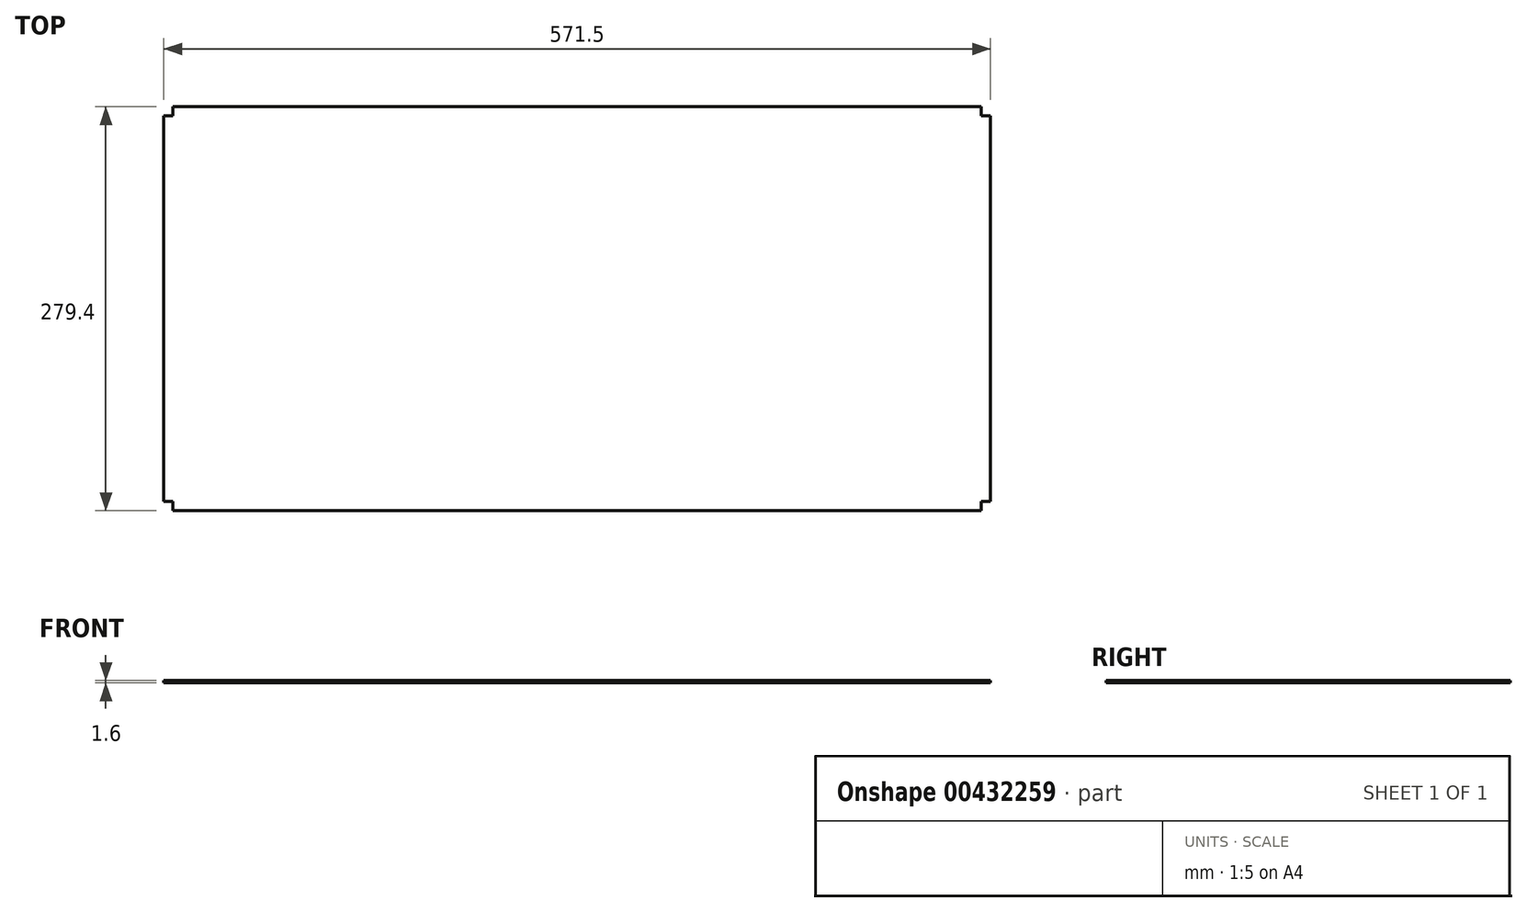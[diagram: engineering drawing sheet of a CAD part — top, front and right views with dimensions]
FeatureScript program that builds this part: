
annotation { "Feature Type Name" : "Feature", "Feature Type Description" : "" }
export const myFeature = defineFeature(function(context is Context, id is Id, definition is map)
    precondition{}
    {
        {
            var Q0;
            Q0=qCreatedBy(makeId("Top.planeOp"),FACE);
            var sketch = newSketch(context, id + "F0", { "sketchPlane" : qUnion([Q0])});
            skLineSegment(sketch, "E0.bottom", {"start": v(279.4, 139.7) * mm, "end": v(-279.4, 139.7) * mm});
            skLineSegment(sketch, "E0.top", {"start": v(279.4, -139.7) * mm, "end": v(-279.4, -139.7) * mm});
            skLineSegment(sketch, "E0.left", {"start": v(285.75, 133.35) * mm, "end": v(285.75, -133.35) * mm});
            skLineSegment(sketch, "E0.right", {"start": v(-285.75, 127) * mm, "end": v(-285.75, -133.35) * mm});
            skPoint(sketch, "E0.middle", {"position": v(0, 0) * mm});
            skPoint(sketch, "E1.orphan", {"position": v(285.75, 139.7) * mm});
            skPoint(sketch, "E2.orphan", {"position": v(-285.75, 139.7) * mm});
            skLineSegment(sketch, "E3.top", {"start": v(-285.75, -133.35) * mm, "end": v(-279.4, -133.35) * mm});
            skLineSegment(sketch, "E3.right", {"start": v(-279.4, -139.7) * mm, "end": v(-279.4, -133.35) * mm});
            skLineSegment(sketch, "E4.top", {"start": v(285.75, -133.35) * mm, "end": v(279.4, -133.35) * mm});
            skLineSegment(sketch, "E4.right", {"start": v(279.4, -139.7) * mm, "end": v(279.4, -133.35) * mm});
            skPoint(sketch, "E4.left.start.orphan", {"position": v(285.75, -139.7) * mm});
            skPoint(sketch, "E5.orphan", {"position": v(-285.75, -139.7) * mm});
            skLineSegment(sketch, "E6.top", {"start": v(-285.75, 133.35) * mm, "end": v(-279.4, 133.35) * mm});
            skLineSegment(sketch, "E6.right", {"start": v(-279.4, 139.7) * mm, "end": v(-279.4, 133.35) * mm});
            skPoint(sketch, "E7.oppositeSnap0", {"position": v(-282.57, 133.35) * mm});
            skLineSegment(sketch, "E7.top", {"start": v(285.75, 133.35) * mm, "end": v(279.4, 133.35) * mm});
            skLineSegment(sketch, "E7.right", {"start": v(279.4, 139.7) * mm, "end": v(279.4, 133.35) * mm});
            skLineSegment(sketch, "E8", {"start": v(-285.75, 127) * mm, "end": v(-285.75, 133.35) * mm});
            skLineSegment(sketch, "E9", {"start": v(-275.24, 139.7) * mm, "end": v(-279.4, 139.7) * mm});
            skLineSegment(sketch, "E10", {"start": v(-279.4, 139.7) * mm, "end": v(-275.24, 139.7) * mm});
            skPoint(sketch, "E11.orphan", {"position": v(-279.4, 146.05) * mm});
            skSolve(sketch);
        }
        {
            var Q0;
            Q0 = qSketchRegion(id + "F0", true);
            extrude(context, id + "F1", {"entities" : qUnion([Q0]), "depth" : 1.6 * mm, "offsetDistance" : 25.4 * mm});
        }
    });
